# Revit family: Flex Pro IP65_0068171-74
name_source: partatom
category: Lighting Fixtures
revit_build: Autodesk Revit 2017 (Build: 20190507_1515(x64)
units: mm (PartAtom-declared; Revit-internal decimal feet)

## family parameters
Cut with Voids When Loaded = No
Host = Face
Light Source = Yes
OmniClass Number = 23.80.70.00
OmniClass Title = Lighting
Part Type = Normal
Room Calculation Point = No
Round Connector Dimension = Use Diameter
Shared = No

## types (4) — shared parameters
Apparent Load = 24 VA
Assembly Code = D5020200
AssetType = Fixed
CABLE_BLEND_SYL = 10 mm  [stored 0.0328084 ft]
CABLE_DIST2_SYL = 2 mm  [stored 0.00656168 ft]
CABLE_DIST_SYL = 2 mm  [stored 0.00656168 ft]
CABLE_END_SYL = 15 mm  [stored 0.0492126 ft]
CABLE_FIX_SYL = 1 mm  [stored 0.00328084 ft]
CABLE_LENGHT_SYL = 995 mm  [stored 3.26444 ft]
ClassificationName = Uniclass2015
ClassificationValue = EF_70_80
Color Filter = 16777215
Default Elevation = 1219 mm
Dimming Lamp Color Temperature Shift = <None>
DocumentationLiterature = http://www.sylvania-lighting.com
ElectricShockClassification = Class III
Emit Shape Visible in Rendering = No
Emit from Circle Diameter = 610 mm
IfcExportAs = IfcLightFixtureType
IfcExportType = IfcLightFixtureType
ImpactProtectionIndex = IK00
IngressProtection = IP65
Keynote = 16500
LED_2_DIST_SYL = 33 mm
LED_CH_L_DEPTH_SYL = 1 mm  [stored 0.00328084 ft]
LED_CH_L_WIDTH_SYL = 2 mm  [stored 0.00656168 ft]
LED_CH_S_DEPTH_SYL = 1 mm  [stored 0.00328084 ft]
LED_CH_S_WIDTH_SYL = 2 mm  [stored 0.00656168 ft]
LED_DIST1_SYL = 11 mm
LED_DIST_SYL = 17 mm
LUM_CAD_W_SYL = 6 mm  [stored 0.019685 ft]
LUM_LENGHT_SYL = 5010 mm  [stored 16.437 ft]
LUM_LENGHT_SYL!!!! = (LUM_LENGHT_SYL-10), MUST BE DIVISIBLE WITH 100
LUM_PROT_SYL = 5 mm  [stored 0.0164042 ft]
LUM_WIDTH_SYL = 4 mm  [stored 0.0131234 ft]
LUM__CAP_SYL = 5 mm  [stored 0.0164042 ft]
Lamp = LED
LampColourRenderingIndex = 90
LampsType = LED
Manufacturer = Feilo Sylvania
ManufacturerName = Feilo Sylvania
Material = other housing
Material_1_SYL = Default New Material
Material_2_SYL = Default
Material_3_SYL = Default New Material(1)
Material_4_SYL = <By Category>
NominalDepth = 10 mm  [stored 0.0328084 ft]
NominalHeight = 4 mm  [stored 0.0131234 ft]
NominalLength = 5000 mm  [stored 16.4042 ft]
PHOTOMETRY1_SYL = 2505 mm  [stored 8.2185 ft]
PHOTOMETRY2_SYL = 4 mm  [stored 0.0131234 ft]
PowerConsumption = 24 W
Tilt Angle = -90.00°
Type Image = <None>
URL = http://www.sylvania-lighting.com
Voltage = 0 V
Weight = 4.0 kg
zero-valued in all types: Cost, PHOTOMETRY3_SYL, PowerFactor

## per-type parameters (varying)
| type | LampColourTemperature | LampNominalLuminous | LuminousEfficacy | Model | ModelNumber | ModelReference | Name | Photometric Web File | TypeName |
| 0068171 FLEX PRO IP65 2100LM 927 | 2700 K | 2100 lm | 88 lm/W | Flex Pro IP65 2100lm 927 | 0068171 | Flex Pro IP65 2100lm 927 | Flex Pro IP65 2100lm 927 | 0068171.ies | Flex Pro IP65 2100lm 927 |
| 0068173 FLEX PRO IP65 2300LM 940 | 4000 K | 2300 lm | 96 lm/W | Flex Pro IP65 2300lm 940 | 0068173 | Flex Pro IP65 2300lm 940 | Flex Pro IP65 2300lm 940 | 0068173.ies | Flex Pro IP65 2300lm 940 |
| 0068172 FLEX PRO IP65 2250LM 930 | 3000 K | 2250 lm | 94 lm/W | Flex Pro IP65 2250lm 930 | 0068172 | Flex Pro IP65 2250lm 930 | Flex Pro IP65 2250lm 930 | 0068172.ies | Flex Pro IP65 2250lm 930 |
| 0068174 FLEX PRO IP65 2300LM 965 | 6500 K | 2300 lm | 96 lm/W | Flex Pro IP65 2300lm 965 | 0068174 | Flex Pro IP65 2300lm 965 | Flex Pro IP65 2300lm 965 | 0068174.ies | Flex Pro IP65 2300lm 965 |

note: [stored X ft] marks values corroborated as IEEE doubles in the binary element streams (Revit-internal decimal feet)

## geometry (parser evidence)
native form markers: Sweep x1
no freeform markers — native parametric forms only
